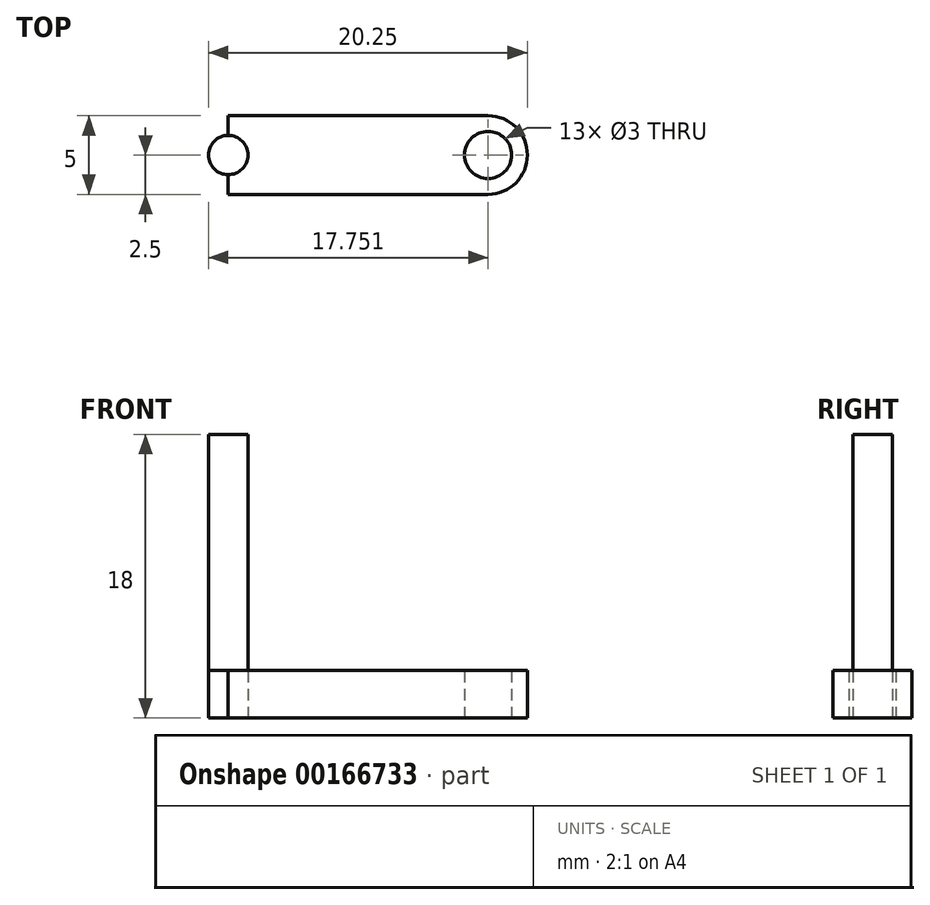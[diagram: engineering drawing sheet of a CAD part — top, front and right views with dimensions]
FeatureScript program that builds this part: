
annotation { "Feature Type Name" : "Feature", "Feature Type Description" : "" }
export const myFeature = defineFeature(function(context is Context, id is Id, definition is map)
    precondition{}
    {
        {
            var Q0;
            Q0=qCreatedBy(makeId("Top.planeOp"),FACE);
            var sketch = newSketch(context, id + "F0", { "sketchPlane" : qUnion([Q0])});
            skPoint(sketch, "E0", {"position": v(0, 0) * mm});
            skLineSegment(sketch, "E1", {"start": v(-8.25, 5) * mm, "end": v(8.25, 5) * mm});
            skPoint(sketch, "E2", {"position": v(0, 5) * mm});
            skLineSegment(sketch, "E3", {"start": v(8.25, 5) * mm, "end": v(8.25, 0) * mm});
            skLineSegment(sketch, "E4", {"start": v(8.25, 0) * mm, "end": v(-8.25, 0) * mm});
            skLineSegment(sketch, "E5", {"start": v(-8.25, 0) * mm, "end": v(-8.25, 5) * mm});
            skPoint(sketch, "E6", {"position": v(8.25, 2.5) * mm});
            skCircle(sketch, "E7", {"center": v(8.25, 2.5) * mm, "radius": 2.5 * mm});
            skPoint(sketch, "E8", {"position": v(-8.25, 2.5) * mm});
            skCircle(sketch, "E9", {"center": v(8.25, 2.5) * mm, "radius": 1.5 * mm});
            skCircle(sketch, "E10", {"center": v(-8.25, 2.5) * mm, "radius": 1.25 * mm});
            skSolve(sketch);
        }
        {
            var Q0;
            Q0 = qSketchRegion(id + "F0", true);
            extrude(context, id + "F1", {"entities" : qUnion([Q0]), "depth" : 3 * mm});
        }
        {
            var Q0;
            {var subQ0=sQuery(id+"F0.wireOp",EDGE,"E10");var subQ1=sQuery(id+"F0.wireOp",EDGE,"E5");var subQ2=makeQuery(id+"F0.imprint","INTERSECT",VERTEX,{"disambiguationData":[OD(0.0)],"derivedFrom":[subQ1,subQ0]});Q0=makeQuery(id+"F0.imprint","IMPRINT",FACE,{"disambiguationData":[TD([[makeQuery(id+"F0.imprint","IMPRINT",EDGE,{"disambiguationData":[TD([[subQ2,-1.0]])],"derivedFrom":subQ1}),-1.0]])]});}
            var Q1;
            {var subQ0=sQuery(id+"F0.wireOp",EDGE,"E10");var subQ1=sQuery(id+"F0.wireOp",EDGE,"E5");var subQ2=makeQuery(id+"F0.imprint","INTERSECT",VERTEX,{"disambiguationData":[OD(0.0)],"derivedFrom":[subQ1,subQ0]});Q1=makeQuery(id+"F0.imprint","IMPRINT",FACE,{"disambiguationData":[TD([[makeQuery(id+"F0.imprint","IMPRINT",EDGE,{"disambiguationData":[TD([[subQ2,-1.0]])],"derivedFrom":subQ1}),1.0]])]});}
            extrude(context, id + "F2", {"entities" : qUnion([Q0, Q1]), "depth" : 18 * mm});
        }
    });
